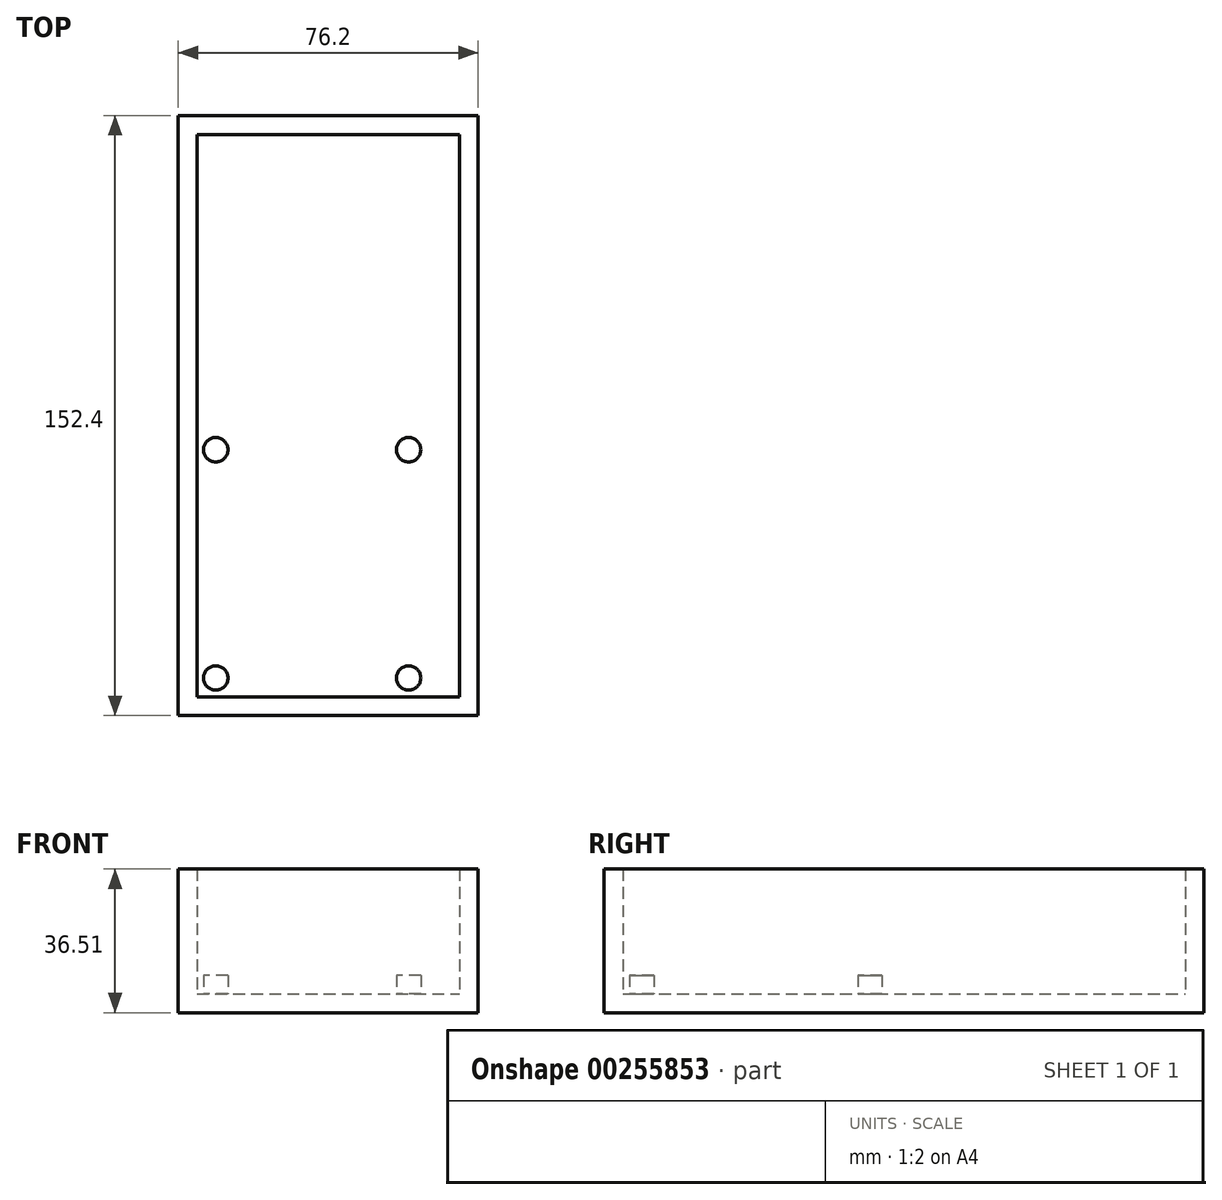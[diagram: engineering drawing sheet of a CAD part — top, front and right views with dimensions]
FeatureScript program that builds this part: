
annotation { "Feature Type Name" : "Feature", "Feature Type Description" : "" }
export const myFeature = defineFeature(function(context is Context, id is Id, definition is map)
    precondition{}
    {
        {
            var Q0;
            Q0=qCreatedBy(makeId("Top.planeOp"),FACE);
            var sketch = newSketch(context, id + "F0", { "sketchPlane" : qUnion([Q0])});
            skLineSegment(sketch, "E0.bottom", {"start": v(-34.49, 100.46) * mm, "end": v(41.71, 100.46) * mm});
            skLineSegment(sketch, "E0.top", {"start": v(-34.49, -51.94) * mm, "end": v(41.71, -51.94) * mm});
            skLineSegment(sketch, "E0.left", {"start": v(-34.49, 100.46) * mm, "end": v(-34.49, -51.94) * mm});
            skLineSegment(sketch, "E0.right", {"start": v(41.71, 100.46) * mm, "end": v(41.71, -51.94) * mm});
            skCircle(sketch, "E1", {"center": v(-24.96, -42.42) * mm, "radius": 3.1 * mm});
            skCircle(sketch, "E2", {"center": v(-24.96, 15.58) * mm, "radius": 3.1 * mm});
            skCircle(sketch, "E3", {"center": v(24.04, -42.42) * mm, "radius": 3.1 * mm});
            skCircle(sketch, "E4", {"center": v(24.04, 15.58) * mm, "radius": 3.1 * mm});
            skLineSegment(sketch, "E5.bottom", {"start": v(-25.46, 39.08) * mm, "end": v(24.54, 39.08) * mm});
            skLineSegment(sketch, "E5.top", {"start": v(-25.46, -45.92) * mm, "end": v(24.54, -45.92) * mm});
            skLineSegment(sketch, "E5.left", {"start": v(-28.46, 36.08) * mm, "end": v(-28.46, -42.92) * mm});
            skLineSegment(sketch, "E5.right", {"start": v(27.54, 36.08) * mm, "end": v(27.54, -42.92) * mm});
            skPoint(sketch, "E6.visualSharp", {"position": v(-28.46, 39.08) * mm});
            skArc(sketch, "E6.filletArc", {"start": v(-25.46, 39.08) * mm, "mid": v(-27.59, 38.2) * mm, "end": v(-28.46, 36.08) * mm});
            skPoint(sketch, "E7.visualSharp", {"position": v(27.54, 39.08) * mm});
            skArc(sketch, "E7.filletArc", {"start": v(27.54, 36.08) * mm, "mid": v(26.66, 38.2) * mm, "end": v(24.54, 39.08) * mm});
            skPoint(sketch, "E8.visualSharp", {"position": v(27.54, -45.92) * mm});
            skArc(sketch, "E8.filletArc", {"start": v(24.54, -45.92) * mm, "mid": v(26.66, -45.04) * mm, "end": v(27.54, -42.92) * mm});
            skPoint(sketch, "E9.visualSharp", {"position": v(-28.46, -45.92) * mm});
            skArc(sketch, "E9.filletArc", {"start": v(-28.46, -42.92) * mm, "mid": v(-27.59, -45.04) * mm, "end": v(-25.46, -45.92) * mm});
            skLineSegment(sketch, "E10.bottom", {"start": v(-29.73, -47.18) * mm, "end": v(36.95, -47.18) * mm});
            skLineSegment(sketch, "E10.top", {"start": v(-29.73, 95.7) * mm, "end": v(36.95, 95.7) * mm});
            skLineSegment(sketch, "E10.left", {"start": v(-29.73, -47.18) * mm, "end": v(-29.73, 95.7) * mm});
            skLineSegment(sketch, "E10.right", {"start": v(36.95, -47.18) * mm, "end": v(36.95, 95.7) * mm});
            skSolve(sketch);
        }
        {
            var Q0;
            Q0 = qSketchRegion(id + "F0", true);
            var Q1;
            Q1=makeQuery(id+"F0.imprint","IMPRINT",FACE,{"disambiguationData":[TD([[makeQuery(id+"F0.imprint","IMPRINT",EDGE,{"derivedFrom":sQuery(id+"F0.wireOp",EDGE,"E5.bottom")}),1.0]])]});
            var Q2;
            Q2=makeQuery(id+"F0.imprint","IMPRINT",FACE,{"disambiguationData":[TD([[makeQuery(id+"F0.imprint","IMPRINT",EDGE,{"derivedFrom":sQuery(id+"F0.wireOp",EDGE,"E1")}),-1.0]])]});
            var Q3;
            Q3=makeQuery(id+"F0.imprint","IMPRINT",FACE,{"disambiguationData":[TD([[makeQuery(id+"F0.imprint","IMPRINT",EDGE,{"derivedFrom":sQuery(id+"F0.wireOp",EDGE,"E4")}),1.0]])]});
            var Q4;
            Q4=makeQuery(id+"F0.imprint","IMPRINT",FACE,{"disambiguationData":[TD([[makeQuery(id+"F0.imprint","IMPRINT",EDGE,{"derivedFrom":sQuery(id+"F0.wireOp",EDGE,"E3")}),1.0]])]});
            var Q5;
            Q5=makeQuery(id+"F0.imprint","IMPRINT",FACE,{"disambiguationData":[TD([[makeQuery(id+"F0.imprint","IMPRINT",EDGE,{"derivedFrom":sQuery(id+"F0.wireOp",EDGE,"E1")}),1.0]])]});
            var Q6;
            Q6=makeQuery(id+"F0.imprint","IMPRINT",FACE,{"disambiguationData":[TD([[makeQuery(id+"F0.imprint","IMPRINT",EDGE,{"derivedFrom":sQuery(id+"F0.wireOp",EDGE,"E2")}),1.0]])]});
            extrude(context, id + "F1", {"entities" : qUnion([Q0, Q1, Q2, Q3, Q4, Q5, Q6]), "oppositeDirection" : true, "depth" : 4.76 * mm});
        }
        {
            var Q0;
            Q0 = qSketchRegion(id + "F0", true);
            extrude(context, id + "F2", {"entities" : qUnion([Q0]), "operationType" : NewBodyOperationType.ADD, "depth" : 31.75 * mm});
        }
        {
            var Q0;
            Q0 = qSketchRegion(id + "F0", true);
            extrude(context, id + "F3", {"entities" : qUnion([Q0]), "operationType" : NewBodyOperationType.ADD, "depth" : 25.4 * mm});
        }
        {
            var Q0;
            Q0=makeQuery(id+"F0.imprint","IMPRINT",FACE,{"disambiguationData":[TD([[makeQuery(id+"F0.imprint","IMPRINT",EDGE,{"derivedFrom":sQuery(id+"F0.wireOp",EDGE,"E4")}),1.0]])]});
            var Q1;
            Q1=makeQuery(id+"F0.imprint","IMPRINT",FACE,{"disambiguationData":[TD([[makeQuery(id+"F0.imprint","IMPRINT",EDGE,{"derivedFrom":sQuery(id+"F0.wireOp",EDGE,"E3")}),1.0]])]});
            var Q2;
            Q2=makeQuery(id+"F0.imprint","IMPRINT",FACE,{"disambiguationData":[TD([[makeQuery(id+"F0.imprint","IMPRINT",EDGE,{"derivedFrom":sQuery(id+"F0.wireOp",EDGE,"E1")}),1.0]])]});
            var Q3;
            Q3=makeQuery(id+"F0.imprint","IMPRINT",FACE,{"disambiguationData":[TD([[makeQuery(id+"F0.imprint","IMPRINT",EDGE,{"derivedFrom":sQuery(id+"F0.wireOp",EDGE,"E2")}),1.0]])]});
            extrude(context, id + "F4", {"entities" : qUnion([Q0, Q1, Q2, Q3]), "operationType" : NewBodyOperationType.ADD, "depth" : 4.76 * mm});
        }
    });
